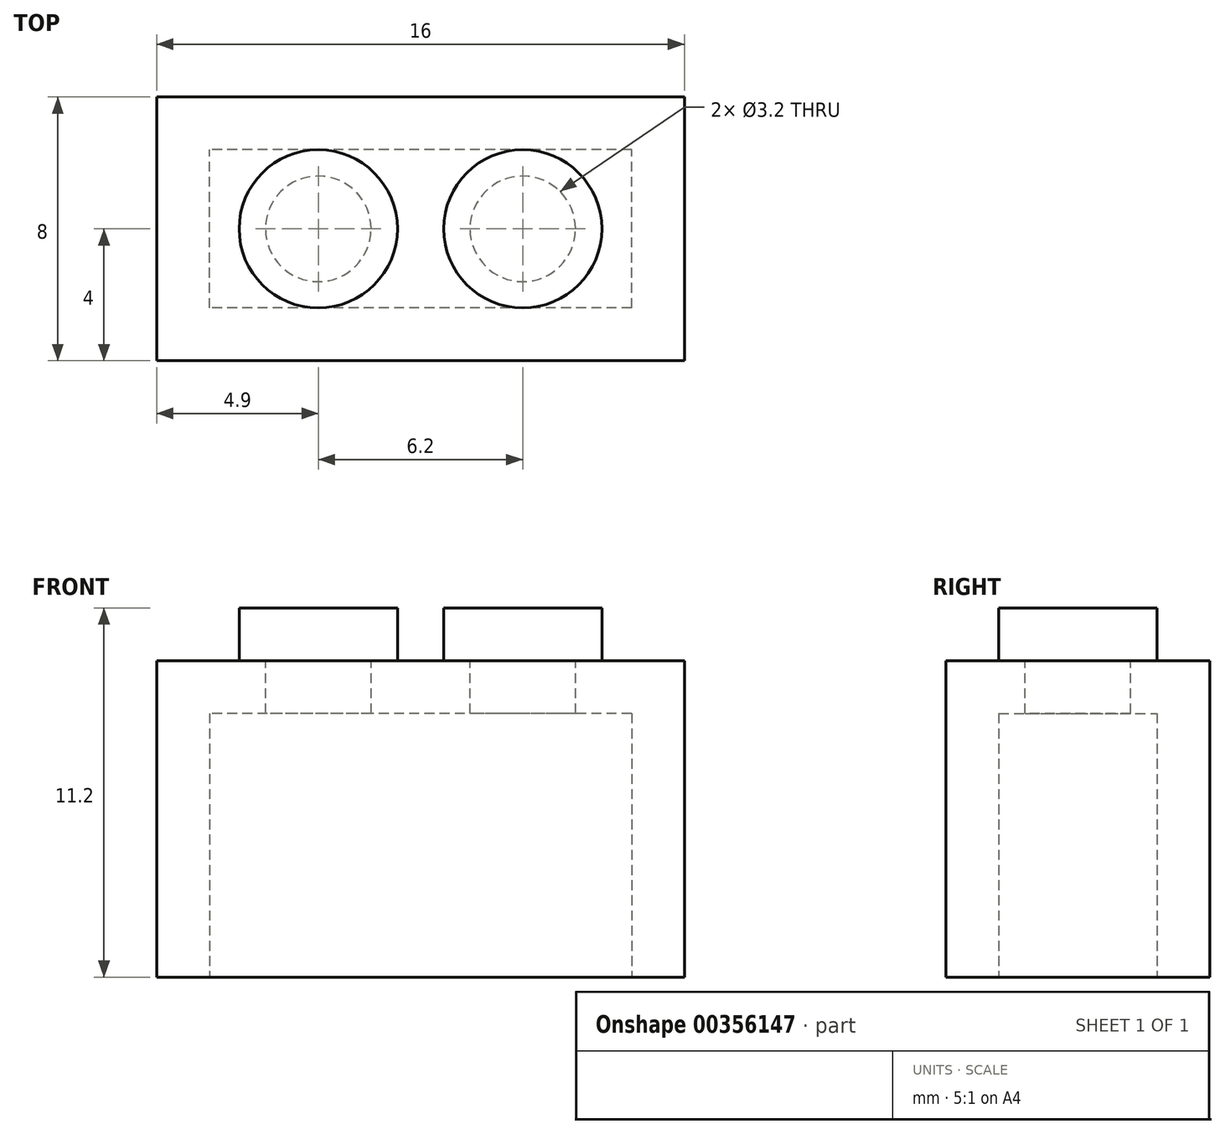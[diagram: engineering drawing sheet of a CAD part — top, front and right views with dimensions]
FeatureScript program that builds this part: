
annotation { "Feature Type Name" : "Feature", "Feature Type Description" : "" }
export const myFeature = defineFeature(function(context is Context, id is Id, definition is map)
    precondition{}
    {
        {
            var Q0;
            Q0=qCreatedBy(makeId("Top.planeOp"),FACE);
            var sketch = newSketch(context, id + "F0", { "sketchPlane" : qUnion([Q0])});
            skLineSegment(sketch, "E0.bottom", {"start": v(8, -4) * mm, "end": v(-8, -4) * mm});
            skLineSegment(sketch, "E0.top", {"start": v(8, 4) * mm, "end": v(-8, 4) * mm});
            skLineSegment(sketch, "E0.left", {"start": v(8, -4) * mm, "end": v(8, 4) * mm});
            skLineSegment(sketch, "E0.right", {"start": v(-8, -4) * mm, "end": v(-8, 4) * mm});
            skPoint(sketch, "E0.middle", {"position": v(0, 0) * mm});
            skLineSegment(sketch, "E1.0", {"start": v(6.4, -2.4) * mm, "end": v(-6.4, -2.4) * mm});
            skLineSegment(sketch, "E1.1", {"start": v(6.4, -2.4) * mm, "end": v(6.4, 2.4) * mm});
            skLineSegment(sketch, "E1.2", {"start": v(6.4, 2.4) * mm, "end": v(-6.4, 2.4) * mm});
            skLineSegment(sketch, "E1.3", {"start": v(-6.4, -2.4) * mm, "end": v(-6.4, 2.4) * mm});
            skSolve(sketch);
        }
        {
            var Q0;
            Q0 = qSketchRegion(id + "F0", true);
            var Q1;
            Q1=makeQuery(id+"F0.imprint","IMPRINT",FACE,{"disambiguationData":[TD([[makeQuery(id+"F0.imprint","IMPRINT",EDGE,{"derivedFrom":sQuery(id+"F0.wireOp",EDGE,"E1.0")}),-1.0]])]});
            extrude(context, id + "F1", {"entities" : qUnion([Q0, Q1]), "depth" : 9.6 * mm});
        }
        {
            var Q0;
            Q0=makeQuery(id+"F0.imprint","IMPRINT",FACE,{"disambiguationData":[TD([[makeQuery(id+"F0.imprint","IMPRINT",EDGE,{"derivedFrom":sQuery(id+"F0.wireOp",EDGE,"E1.0")}),-1.0]])]});
            extrude(context, id + "F2", {"entities" : qUnion([Q0]), "operationType" : NewBodyOperationType.REMOVE, "depth" : 8 * mm});
        }
        {
            var Q0;
            Q0=makeQuery(id+"F1.opExtrude","CAP_FACE",FACE,{"disambiguationData":[OSD([sQuery(id+"F0.wireOp",EDGE,"E0.bottom"),sQuery(id+"F0.wireOp",EDGE,"E0.top"),sQuery(id+"F0.wireOp",EDGE,"E0.left"),sQuery(id+"F0.wireOp",EDGE,"E0.right")])],"isStart":false});
            var sketch = newSketch(context, id + "F3", { "sketchPlane" : qUnion([Q0])});
            skCircle(sketch, "E2", {"center": v(-3.1, 0) * mm, "radius": 1.6 * mm});
            skCircle(sketch, "E3", {"center": v(3.1, 0) * mm, "radius": 1.6 * mm});
            skSolve(sketch);
        }
        {
            var Q0;
            Q0 = qSketchRegion(id + "F3", true);
            extrude(context, id + "F4", {"entities" : qUnion([Q0]), "operationType" : NewBodyOperationType.REMOVE, "oppositeDirection" : true, "depth" : 3.2 * mm});
        }
        {
            var Q0;
            Q0=makeQuery(id+"F1.opExtrude","CAP_FACE",FACE,{"disambiguationData":[OSD([sQuery(id+"F0.wireOp",EDGE,"E0.bottom"),sQuery(id+"F0.wireOp",EDGE,"E0.top"),sQuery(id+"F0.wireOp",EDGE,"E0.left"),sQuery(id+"F0.wireOp",EDGE,"E0.right")])],"isStart":false});
            var sketch = newSketch(context, id + "F5", { "sketchPlane" : qUnion([Q0])});
            skCircle(sketch, "E4", {"center": v(-3.1, 0) * mm, "radius": 2.4 * mm});
            skCircle(sketch, "E5", {"center": v(3.1, 0) * mm, "radius": 2.4 * mm});
            skSolve(sketch);
        }
        {
            var Q0;
            Q0 = qSketchRegion(id + "F5", true);
            extrude(context, id + "F6", {"entities" : qUnion([Q0]), "depth" : 1.6 * mm});
        }
        {
            var Q0;
            Q0=makeQuery(id+"F0.imprint","IMPRINT",FACE,{"disambiguationData":[TD([[makeQuery(id+"F0.imprint","IMPRINT",EDGE,{"derivedFrom":sQuery(id+"F0.wireOp",EDGE,"E1.0")}),-1.0]])]});
            var sketch = newSketch(context, id + "F7", { "sketchPlane" : qUnion([Q0])});
            skLineSegment(sketch, "E6", {"start": v(0, -2.24) * mm, "end": v(0, 2.36) * mm});
            skSolve(sketch);
        }
        {
            var Q0;
            Q0=sQuery(id+"F7.wireOp",EDGE,"E6");
            extrude(context, id + "F8", {"bodyType" : ToolBodyType.SURFACE, "surfaceEntities" : qUnion([Q0]), "depth" : 8.9 * mm});
        }
    });
